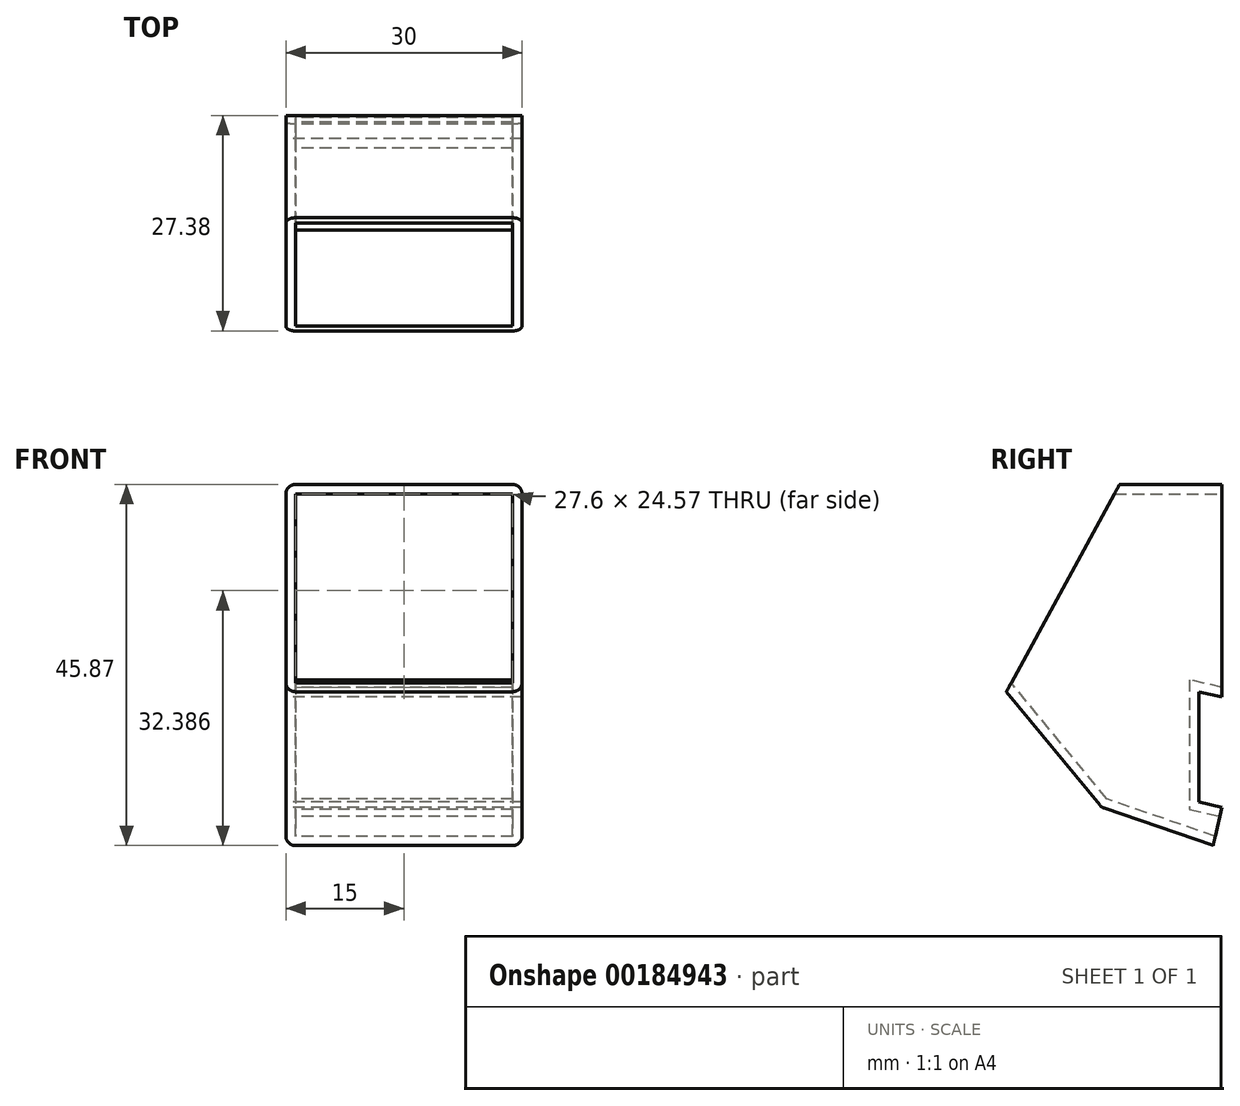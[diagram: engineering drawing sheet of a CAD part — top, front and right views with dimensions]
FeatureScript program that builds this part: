
annotation { "Feature Type Name" : "Feature", "Feature Type Description" : "" }
export const myFeature = defineFeature(function(context is Context, id is Id, definition is map)
    precondition{}
    {
        {
            var Q0;
            Q0=qCreatedBy(makeId("Right.planeOp"),FACE);
            var sketch = newSketch(context, id + "F0", { "sketchPlane" : qUnion([Q0])});
            skLineSegment(sketch, "E0", {"start": v(0, 0) * mm, "end": v(-2.92, 0.67) * mm});
            skLineSegment(sketch, "E1", {"start": v(-2.92, 0.67) * mm, "end": v(-2.92, -13.33) * mm});
            skLineSegment(sketch, "E2", {"start": v(-2.92, -13.33) * mm, "end": v(0, -14) * mm});
            skLineSegment(sketch, "E3", {"start": v(0, -14) * mm, "end": v(-1.12, -18.87) * mm});
            skLineSegment(sketch, "E4", {"start": v(-1.12, -18.87) * mm, "end": v(-15.3, -14) * mm});
            skLineSegment(sketch, "E5", {"start": v(-15.3, -14) * mm, "end": v(-27.38, 0.67) * mm});
            skLineSegment(sketch, "E6", {"start": v(-27.38, 0.67) * mm, "end": v(-13, 27) * mm});
            skLineSegment(sketch, "E7", {"start": v(-13, 27) * mm, "end": v(0, 27) * mm});
            skLineSegment(sketch, "E8", {"start": v(0, 27) * mm, "end": v(0, 0) * mm});
            skSolve(sketch);
        }
        {
            var Q0;
            Q0 = qSketchRegion(id + "F0", true);
            extrude(context, id + "F1", {"entities" : qUnion([Q0]), "endBound" : BoundingType.SYMMETRIC, "depth" : 30 * mm});
        }
        {
            var Q0;
            Q0=makeQuery(id+"F1.opExtrude","SWEPT_FACE",FACE,{"disambiguationData":[OSD([sQuery(id+"F0.wireOp",EDGE,"E8")])]});
            var Q1;
            Q1=makeQuery(id+"F1.opExtrude","SWEPT_FACE",FACE,{"disambiguationData":[OSD([sQuery(id+"F0.wireOp",EDGE,"E3")])]});
            var Q2;
            Q2=makeQuery(id+"F1.opExtrude","SWEPT_FACE",FACE,{"disambiguationData":[OSD([sQuery(id+"F0.wireOp",EDGE,"E6")])]});
            shell(context, id + "F2", {"entities" : qUnion([Q0, Q1, Q2]), "thickness" : 1.2 * mm});
        }
        {
            var Q0;
            Q0=makeQuery(id+"F1.opExtrude","CAP_EDGE",EDGE,{"disambiguationData":[OSD([sQuery(id+"F0.wireOp",EDGE,"E7")])],"isStart":true});
            var Q1;
            Q1=makeQuery(id+"F1.opExtrude","CAP_EDGE",EDGE,{"disambiguationData":[OSD([sQuery(id+"F0.wireOp",EDGE,"E7")])],"isStart":false});
            var Q2;
            Q2=makeQuery(id+"F1.opExtrude","CAP_EDGE",EDGE,{"disambiguationData":[OSD([sQuery(id+"F0.wireOp",EDGE,"E4")])],"isStart":true});
            var Q3;
            Q3=makeQuery(id+"F1.opExtrude","SWEPT_EDGE",EDGE,{"disambiguationData":[OSD([sQuery(id+"F0.wireOp",EDGE,"E4"),sQuery(id+"F0.wireOp",EDGE,"E5")])]});
            var Q4;
            Q4=makeQuery(id+"F1.opExtrude","CAP_EDGE",EDGE,{"disambiguationData":[OSD([sQuery(id+"F0.wireOp",EDGE,"E5")])],"isStart":true});
            var Q5;
            Q5=makeQuery(id+"F1.opExtrude","CAP_EDGE",EDGE,{"disambiguationData":[OSD([sQuery(id+"F0.wireOp",EDGE,"E4")])],"isStart":false});
            var Q6;
            Q6=makeQuery(id+"F1.opExtrude","CAP_EDGE",EDGE,{"disambiguationData":[OSD([sQuery(id+"F0.wireOp",EDGE,"E5")])],"isStart":false});
            fillet(context, id + "F3", {"entities" : qUnion([Q0, Q1, Q2, Q3, Q4, Q5, Q6]), "radius" : 1.2 * mm, "tangentPropagation" : true, "allowEdgeOverflow" : false});
        }
    });
